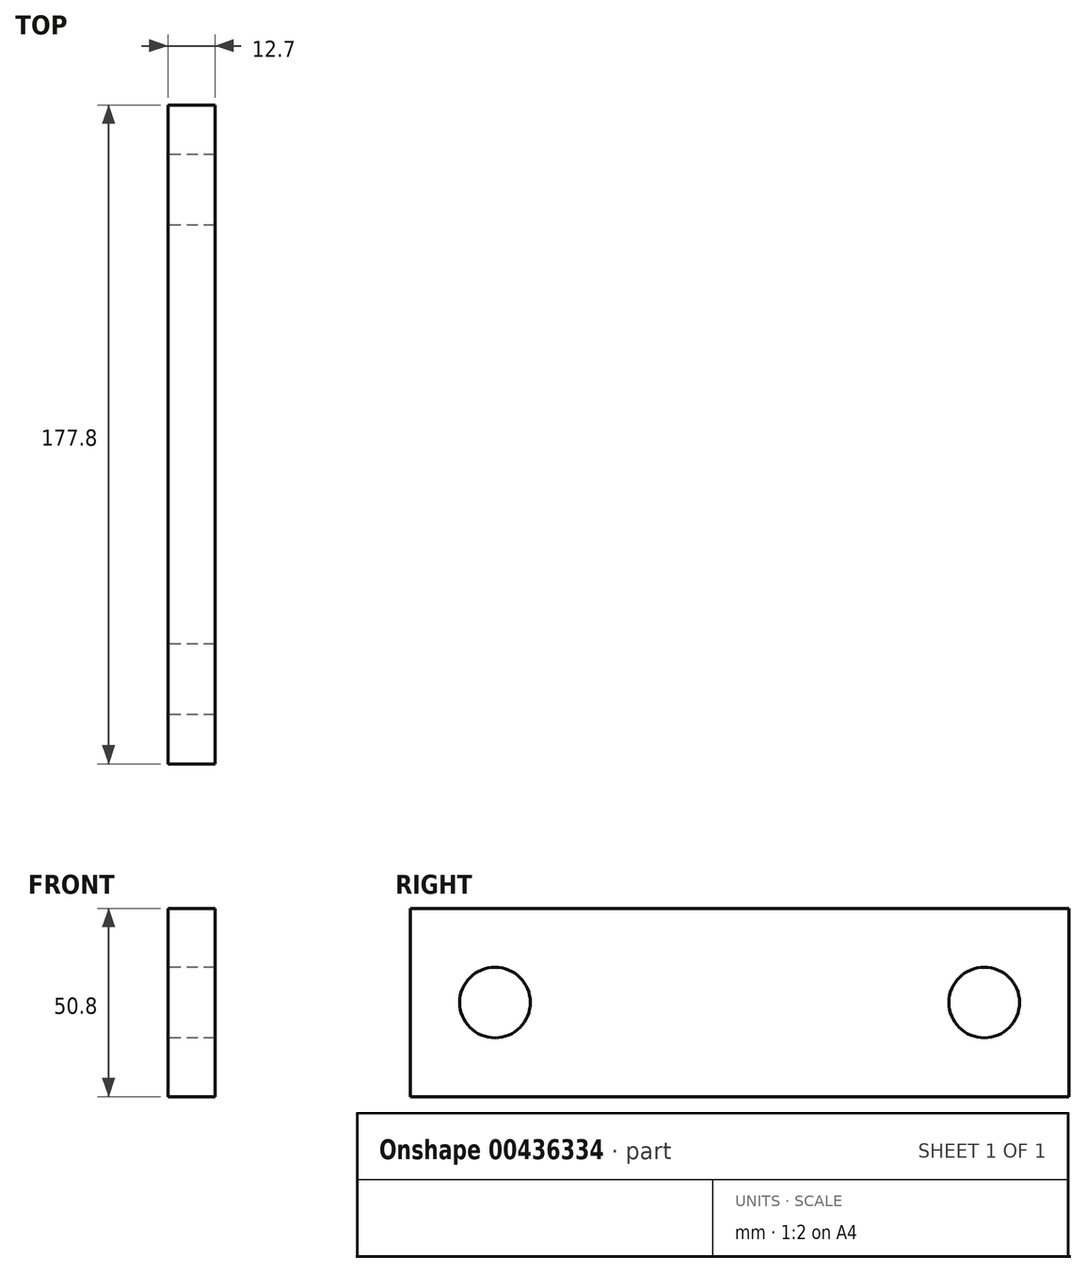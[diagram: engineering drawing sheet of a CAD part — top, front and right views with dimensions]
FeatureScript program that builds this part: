
annotation { "Feature Type Name" : "Feature", "Feature Type Description" : "" }
export const myFeature = defineFeature(function(context is Context, id is Id, definition is map)
    precondition{}
    {
        {
            var Q0;
            Q0=qCreatedBy(makeId("Right.planeOp"),FACE);
            var sketch = newSketch(context, id + "F0", { "sketchPlane" : qUnion([Q0])});
            skLineSegment(sketch, "E0.bottom", {"start": v(88.9, 25.4) * mm, "end": v(-88.9, 25.4) * mm});
            skLineSegment(sketch, "E0.top", {"start": v(88.9, -25.4) * mm, "end": v(-88.9, -25.4) * mm});
            skLineSegment(sketch, "E0.left", {"start": v(88.9, 25.4) * mm, "end": v(88.9, -25.4) * mm});
            skLineSegment(sketch, "E0.right", {"start": v(-88.9, 25.4) * mm, "end": v(-88.9, -25.4) * mm});
            skPoint(sketch, "E0.middle", {"position": v(0, 0) * mm});
            skCircle(sketch, "E1", {"center": v(-66.04, 0) * mm, "radius": 9.53 * mm});
            skCircle(sketch, "E2", {"center": v(66.04, 0) * mm, "radius": 9.53 * mm});
            skSolve(sketch);
        }
        {
            var Q0;
            Q0 = qSketchRegion(id + "F0", true);
            extrude(context, id + "F1", {"entities" : qUnion([Q0]), "endBound" : BoundingType.SYMMETRIC, "depth" : 12.7 * mm});
        }
    });
